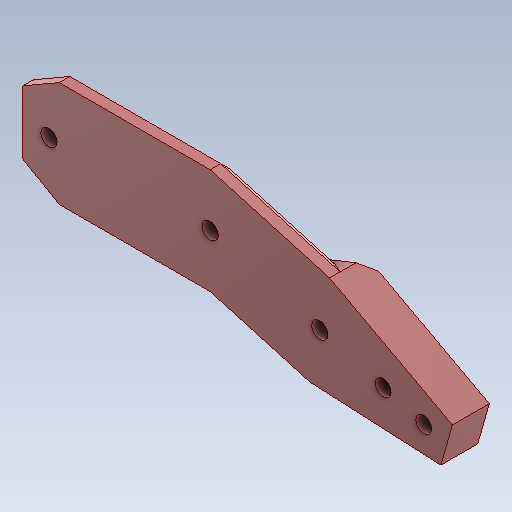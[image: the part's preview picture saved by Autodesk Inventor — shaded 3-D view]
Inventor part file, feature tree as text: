
AUTODESK INVENTOR PART (.ipt)
format: ipt  version: 2020 (Build 240168000, 168)  size: 180,224 bytes
history: native  units: in
note: dims shown in document units (in); Inventor stores cm internally (conversion verified against a paired STEP export)
features: sketch x4, other x3
ambient origin geometry x8: Origin, YZ Plane, XZ Plane, XY Plane, X Axis, Y Axis, Z Axis, Center Point
bodies: Solid1 (feature_tree)
feature tree (7):
  other  "FibulaBot.ipt"
  other  "Solid1::FibulaBot.ipt"
  other  "TaggingFeature1"
  sketch  "Sketch1"  dims[d0=0.3937in]
  sketch  "Sketch3"
  sketch  "Sketch4"
  sketch  "Sketch5"
